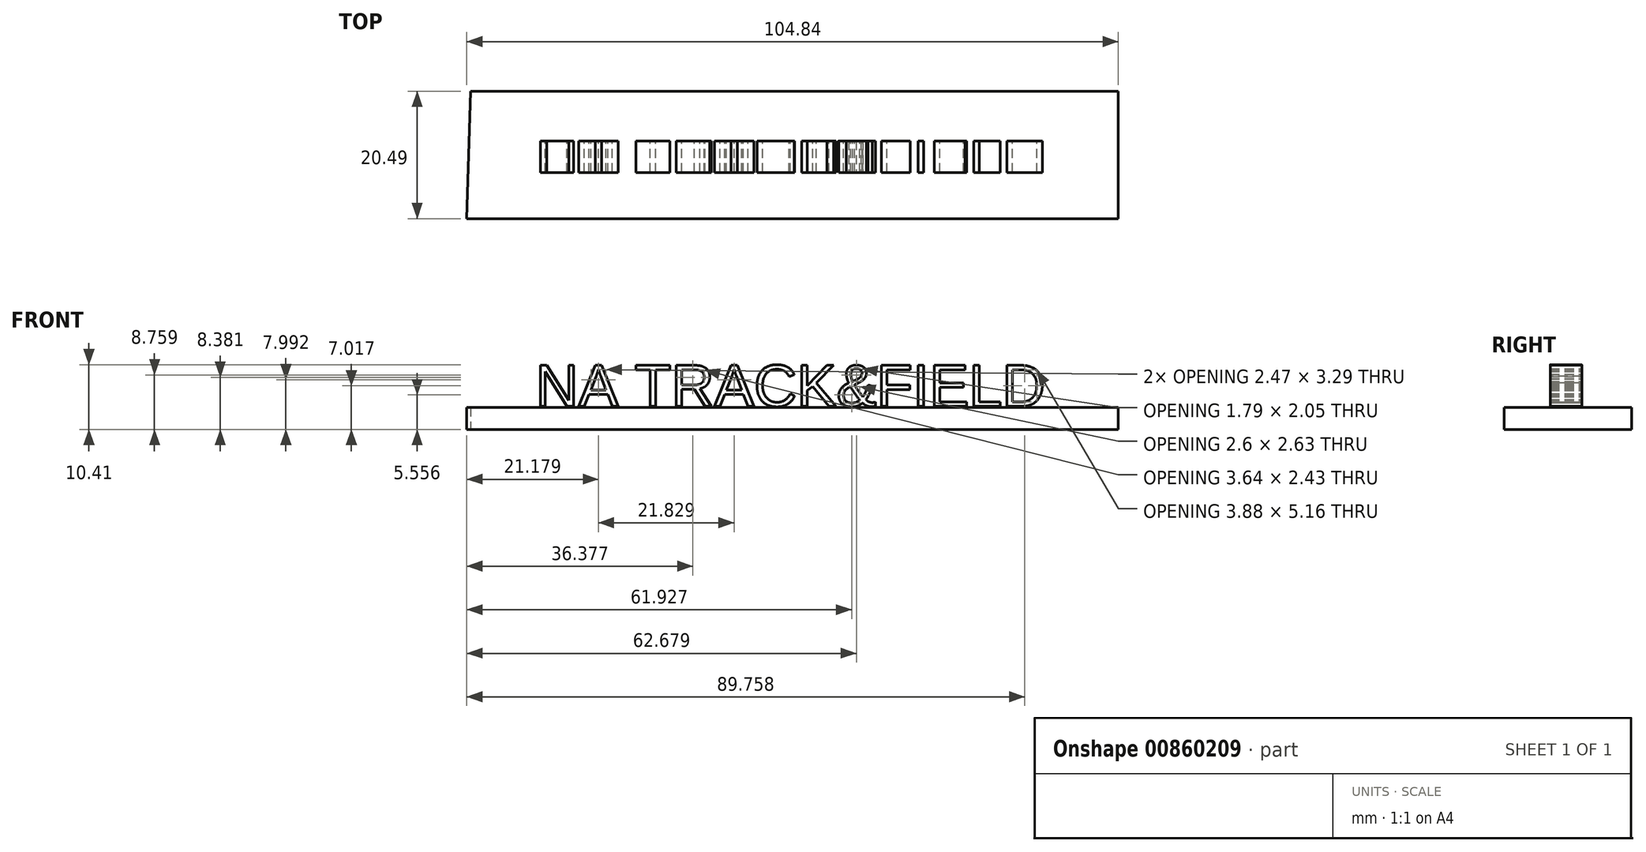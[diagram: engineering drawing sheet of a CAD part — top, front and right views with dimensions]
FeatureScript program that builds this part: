
annotation { "Feature Type Name" : "Feature", "Feature Type Description" : "" }
export const myFeature = defineFeature(function(context is Context, id is Id, definition is map)
    precondition{}
    {
        {
            var Q0;
            Q0=qCreatedBy(makeId("Top.planeOp"),FACE);
            var sketch = newSketch(context, id + "F0", { "sketchPlane" : qUnion([Q0])});
            skLineSegment(sketch, "E0", {"start": v(-52.91, -12.51) * mm, "end": v(51.93, -12.51) * mm});
            skLineSegment(sketch, "E1", {"start": v(51.93, -12.51) * mm, "end": v(51.93, 7.98) * mm});
            skLineSegment(sketch, "E2", {"start": v(51.93, 7.98) * mm, "end": v(-52.32, 7.98) * mm});
            skLineSegment(sketch, "E3", {"start": v(-52.32, 7.98) * mm, "end": v(-52.91, -12.51) * mm});
            skSolve(sketch);
        }
        {
            var Q0;
            Q0 = qSketchRegion(id + "F0", true);
            extrude(context, id + "F1", {"entities" : qUnion([Q0]), "depth" : 3.56 * mm, "offsetDistance" : 25.4 * mm});
        }
        {
            var Q0;
            Q0=qCreatedBy(makeId("Front.planeOp"),FACE);
            var sketch = newSketch(context, id + "F2", { "sketchPlane" : qUnion([Q0])});
            skText(sketch, "E4", { "text": "NA TRACK&FIELD\n", "fontName": "Arimo-Regular.ttf"});
            const initialGuessF2  = {"E4": [-0.04186, 0.00372, 1, 0, 0.0069]};
            skSetInitialGuess(sketch, initialGuessF2);
            skSolve(sketch);
        }
        {
            var Q0;
            Q0 = qSketchRegion(id + "F2", true);
            extrude(context, id + "F3", {"entities" : qUnion([Q0]), "depth" : 5.08 * mm, "offsetDistance" : 25.4 * mm});
        }
    });
